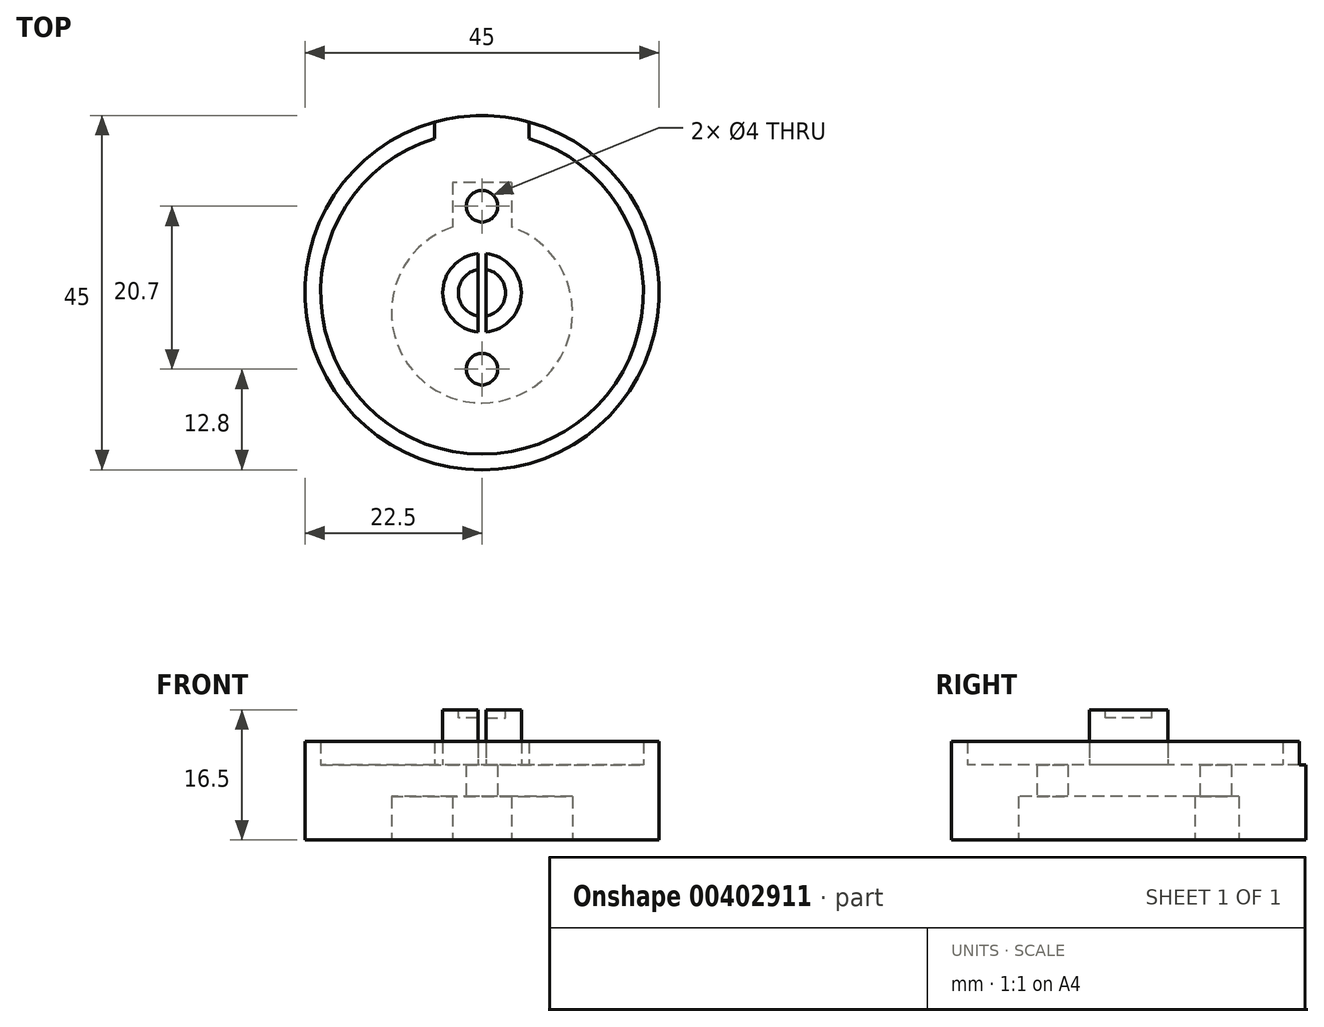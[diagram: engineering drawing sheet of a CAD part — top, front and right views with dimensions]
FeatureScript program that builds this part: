
annotation { "Feature Type Name" : "Feature", "Feature Type Description" : "" }
export const myFeature = defineFeature(function(context is Context, id is Id, definition is map)
    precondition{}
    {
        {
            var Q0;
            Q0=qCreatedBy(makeId("Top.planeOp"),FACE);
            var sketch = newSketch(context, id + "F0", { "sketchPlane" : qUnion([Q0])});
            skCircle(sketch, "E0", {"center": v(0, 0) * mm, "radius": 22.5 * mm});
            skLineSegment(sketch, "E1", {"start": v(3.75, 14) * mm, "end": v(-3.75, 14) * mm});
            skLineSegment(sketch, "E2", {"start": v(0, 0) * mm, "end": v(0, -14) * mm, "construction": true});
            skLineSegment(sketch, "E3", {"start": v(0, -14) * mm, "end": v(-17.61, -14) * mm, "construction": true});
            skLineSegment(sketch, "E4", {"start": v(-3.75, 14) * mm, "end": v(-3.75, 8.37) * mm});
            skLineSegment(sketch, "E5", {"start": v(3.75, 14) * mm, "end": v(3.75, 8.37) * mm});
            skLineSegment(sketch, "E6", {"start": v(0, 14) * mm, "end": v(0, 0) * mm, "construction": true});
            skCircle(sketch, "E7", {"center": v(0, -2.5) * mm, "radius": 11.5 * mm});
            skLineSegment(sketch, "E8", {"start": v(0, 14) * mm, "end": v(0, 22.5) * mm, "construction": true});
            skLineSegment(sketch, "E9", {"start": v(0, -14) * mm, "end": v(0, -22.5) * mm, "construction": true});
            skSolve(sketch);
        }
        {
            var Q0;
            Q0=makeQuery(id+"F0.imprint","IMPRINT",FACE,{"disambiguationData":[TD([[makeQuery(id+"F0.imprint","IMPRINT",EDGE,{"derivedFrom":sQuery(id+"F0.wireOp",EDGE,"E0")}),1.0]])]});
            extrude(context, id + "F1", {"entities" : qUnion([Q0]), "depth" : 5.5 * mm});
        }
        {
            var Q0;
            Q0=makeQuery(id+"F1.opExtrude","CAP_FACE",FACE,{"disambiguationData":[OSD([sQuery(id+"F0.wireOp",EDGE,"E0"),sQuery(id+"F0.wireOp",EDGE,"d1SFJXsT-dEDW-4JRq-AfPg-EI6cgoUd3JrW"),sQuery(id+"F0.wireOp",EDGE,"E1"),sQuery(id+"F0.wireOp",EDGE,"E4"),sQuery(id+"F0.wireOp",EDGE,"E5")])],"isStart":false});
            var sketch = newSketch(context, id + "F2", { "sketchPlane" : qUnion([Q0])});
            skCircle(sketch, "E10", {"center": v(0, 0) * mm, "radius": 22.5 * mm});
            skCircle(sketch, "E11", {"center": v(0, 11) * mm, "radius": 2 * mm});
            skCircle(sketch, "E12", {"center": v(0, -9.7) * mm, "radius": 2 * mm});
            skLineSegment(sketch, "E13", {"start": v(0, 11) * mm, "end": v(0, 0) * mm, "construction": true});
            skLineSegment(sketch, "E14", {"start": v(0, -9.7) * mm, "end": v(0, 0) * mm, "construction": true});
            skSolve(sketch);
        }
        {
            var Q0;
            Q0 = qSketchRegion(id + "F2", true);
            extrude(context, id + "F3", {"entities" : qUnion([Q0]), "operationType" : NewBodyOperationType.ADD, "depth" : 4 * mm});
        }
        {
            var Q0;
            Q0=makeQuery(id+"F3.opExtrude","CAP_FACE",FACE,{"disambiguationData":[OSD([sQuery(id+"F2.wireOp",EDGE,"E10"),sQuery(id+"F2.wireOp",EDGE,"E11"),sQuery(id+"F2.wireOp",EDGE,"E12")])],"isStart":false});
            var sketch = newSketch(context, id + "F4", { "sketchPlane" : qUnion([Q0])});
            skCircle(sketch, "E15", {"center": v(0, 0) * mm, "radius": 22.5 * mm});
            skCircle(sketch, "E16", {"center": v(0, 0) * mm, "radius": 20.5 * mm});
            skCircle(sketch, "E17", {"center": v(0, 0) * mm, "radius": 5 * mm});
            skLineSegment(sketch, "E18", {"start": v(-0.5, 4.97) * mm, "end": v(-0.5, -4.97) * mm});
            skLineSegment(sketch, "E19", {"start": v(0.5, 4.97) * mm, "end": v(0.5, -4.97) * mm});
            skLineSegment(sketch, "E20", {"start": v(0, 0) * mm, "end": v(0.5, 0) * mm, "construction": true});
            skLineSegment(sketch, "E21", {"start": v(0, 0) * mm, "end": v(-0.5, 0) * mm, "construction": true});
            skLineSegment(sketch, "E22", {"start": v(-6, 21.69) * mm, "end": v(-6, 16.69) * mm});
            skLineSegment(sketch, "E23", {"start": v(6, 21.69) * mm, "end": v(6, 16.69) * mm});
            skLineSegment(sketch, "E24", {"start": v(6, 16.69) * mm, "end": v(-6, 16.69) * mm});
            skLineSegment(sketch, "E25", {"start": v(0, 0) * mm, "end": v(0, 16.69) * mm, "construction": true});
            skSolve(sketch);
        }
        {
            var Q0;
            {var subQ0=sQuery(id+"F4.wireOp",EDGE,"E22");var subQ1=sQuery(id+"F4.wireOp",EDGE,"E15");var subQ2=makeQuery(id+"F4.imprint","INTERSECT",VERTEX,{"derivedFrom":[subQ1,subQ0]});Q0=makeQuery(id+"F4.imprint","IMPRINT",FACE,{"disambiguationData":[TD([[makeQuery(id+"F4.imprint","IMPRINT",EDGE,{"disambiguationData":[TD([[subQ2,-1.0]])],"derivedFrom":subQ1}),1.0]])]});}
            extrude(context, id + "F5", {"entities" : qUnion([Q0]), "operationType" : NewBodyOperationType.ADD, "depth" : 3 * mm});
        }
        {
            var Q0;
            {var subQ0=sQuery(id+"F4.wireOp",EDGE,"E18");Q0=makeQuery(id+"F4.imprint","IMPRINT",FACE,{"disambiguationData":[TD([[makeQuery(id+"F4.imprint","IMPRINT",EDGE,{"derivedFrom":subQ0}),-1.0]])]});}
            var Q1;
            {var subQ0=sQuery(id+"F4.wireOp",EDGE,"E19");Q1=makeQuery(id+"F4.imprint","IMPRINT",FACE,{"disambiguationData":[TD([[makeQuery(id+"F4.imprint","IMPRINT",EDGE,{"derivedFrom":subQ0}),1.0]])]});}
            extrude(context, id + "F6", {"entities" : qUnion([Q0, Q1]), "operationType" : NewBodyOperationType.ADD, "depth" : 7 * mm});
        }
        {
            var Q0;
            Q0=makeQuery(id+"F6.opExtrude","CAP_FACE",FACE,{"disambiguationData":[OSD([sQuery(id+"F4.wireOp",EDGE,"E17"),sQuery(id+"F4.wireOp",EDGE,"E18")])],"isStart":false});
            var sketch = newSketch(context, id + "F7", { "sketchPlane" : qUnion([Q0])});
            skArc(sketch, "E26.0", {"start": v(-0.5, 2.96) * mm, "mid": v(-3, 0) * mm, "end": v(-0.5, -2.96) * mm});
            skLineSegment(sketch, "E27", {"start": v(-0.5, 0) * mm, "end": v(-3, 0) * mm, "construction": true});
            skSolve(sketch);
        }
        {
            var Q0;
            {var subQ0=sQuery(id+"F7.wireOp",EDGE,"E26.0");Q0=makeQuery(id+"F7.imprint","IMPRINT",FACE,{"disambiguationData":[TD([[makeQuery(id+"F7.imprint","IMPRINT",EDGE,{"derivedFrom":subQ0}),1.0]])]});}
            extrude(context, id + "F8", {"entities" : qUnion([Q0]), "operationType" : NewBodyOperationType.REMOVE, "oppositeDirection" : true, "depth" : 1 * mm});
        }
        {
            var Q0;
            Q0=makeQuery(id+"F6.opExtrude","CAP_FACE",FACE,{"disambiguationData":[OSD([sQuery(id+"F4.wireOp",EDGE,"E17"),sQuery(id+"F4.wireOp",EDGE,"E19")])],"isStart":false});
            var sketch = newSketch(context, id + "F9", { "sketchPlane" : qUnion([Q0])});
            skArc(sketch, "E28.0", {"start": v(0.5, -2.96) * mm, "mid": v(3, 0) * mm, "end": v(0.5, 2.96) * mm});
            skLineSegment(sketch, "E29", {"start": v(3, 0) * mm, "end": v(0.5, 0) * mm, "construction": true});
            skSolve(sketch);
        }
        {
            var Q0;
            {var subQ0=sQuery(id+"F9.wireOp",EDGE,"E28.0");Q0=makeQuery(id+"F9.imprint","IMPRINT",FACE,{"disambiguationData":[TD([[makeQuery(id+"F9.imprint","IMPRINT",EDGE,{"derivedFrom":subQ0}),1.0]])]});}
            extrude(context, id + "F10", {"entities" : qUnion([Q0]), "operationType" : NewBodyOperationType.REMOVE, "oppositeDirection" : true, "depth" : 1 * mm});
        }
    });
